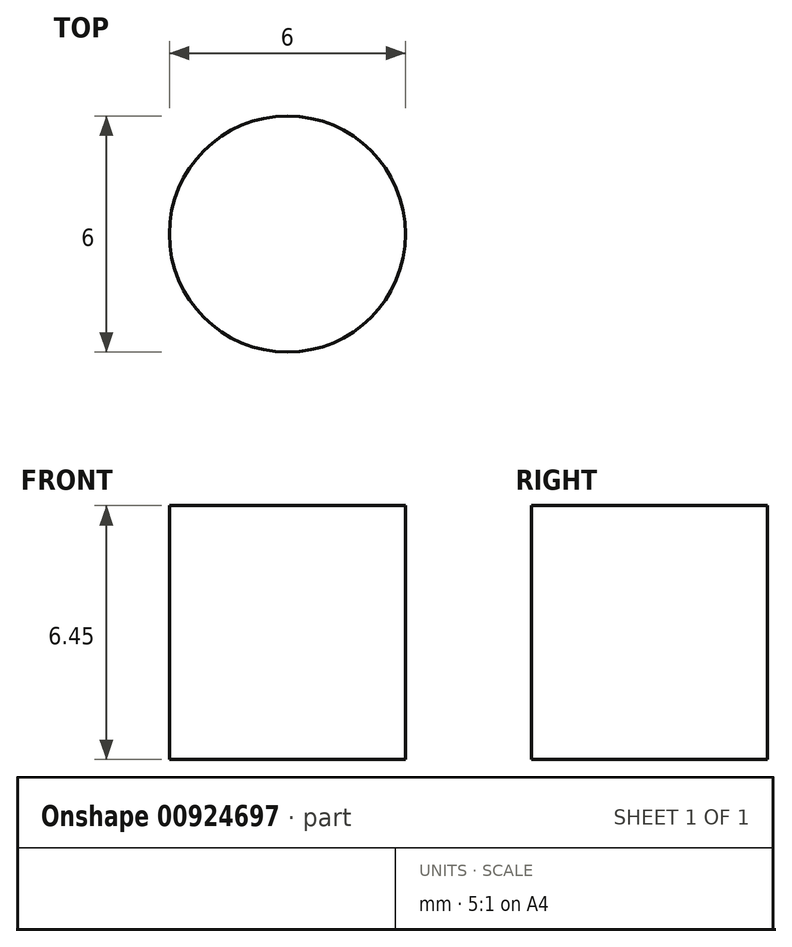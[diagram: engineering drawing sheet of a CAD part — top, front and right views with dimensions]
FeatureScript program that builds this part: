
annotation { "Feature Type Name" : "Feature", "Feature Type Description" : "" }
export const myFeature = defineFeature(function(context is Context, id is Id, definition is map)
    precondition{}
    {
        {
            var Q0;
            Q0=qCreatedBy(makeId("Top.planeOp"),FACE);
            var sketch = newSketch(context, id + "F0", { "sketchPlane" : qUnion([Q0])});
            skCircle(sketch, "E0", {"center": v(0, 0) * mm, "radius": 3 * mm});
            skSolve(sketch);
        }
        {
            var Q0;
            Q0=makeQuery(id+"F0.imprint","IMPRINT",FACE,{"disambiguationData":[TD([[makeQuery(id+"F0.imprint","IMPRINT",EDGE,{"derivedFrom":sQuery(id+"F0.wireOp",EDGE,"E0")}),1.0]])]});
            extrude(context, id + "F1", {"entities" : qUnion([Q0]), "depth" : (11.25 - 4.8) * mm, "offsetDistance" : 25 * mm});
        }
    });
